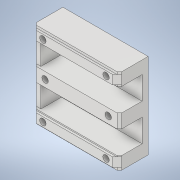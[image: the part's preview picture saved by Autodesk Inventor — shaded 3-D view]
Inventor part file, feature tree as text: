
AUTODESK INVENTOR PART (.ipt)
format: ipt  version: 2020 (Build 240168000, 168)  size: 205,824 bytes
history: native  units: mm
features: extrude x5, sketch x5, chamfer x3, other x2, pattern_linear x1
ambient origin geometry x8: Origin, YZ Plane, XZ Plane, XY Plane, X Axis, Y Axis, Z Axis, Center Point
bodies: Body1 (feature_tree)
feature tree (16):
  other  "Bryła1"
  extrude  "Wyciągnięcie proste1"  Depth=74.0mm
  extrude  "Wyciągnięcie proste2"  Depth=74.0mm
  extrude  "Wyciągnięcie proste3"  Depth=25.0mm TaperAngle=0.0deg
  other  "Płaszczyzna konstrukcyjna1"
  extrude  "Wyciągnięcie proste5"  Depth=20.0mm
  pattern_linear  "Szyk prostokątny1"  Count1=2  [1 undecoded]
  chamfer  "Faza1"  Distance=11.0mm
  chamfer  "Faza2"  Distance=11.0mm
  chamfer  "Faza3"  Distance=19.8mm
  extrude  "Wyciągnięcie proste6"  Depth=2.05mm
  sketch  "Szkic1"
  sketch  "Szkic2"
  sketch  "Szkic3"
  sketch  "Szkic5"
  sketch  "Szkic6"
note: 1 required parameter value undecoded (feature->parameter linkage not recoverable at this tier; creation-order binding heuristic only, values carry confidence <= 0.55)
